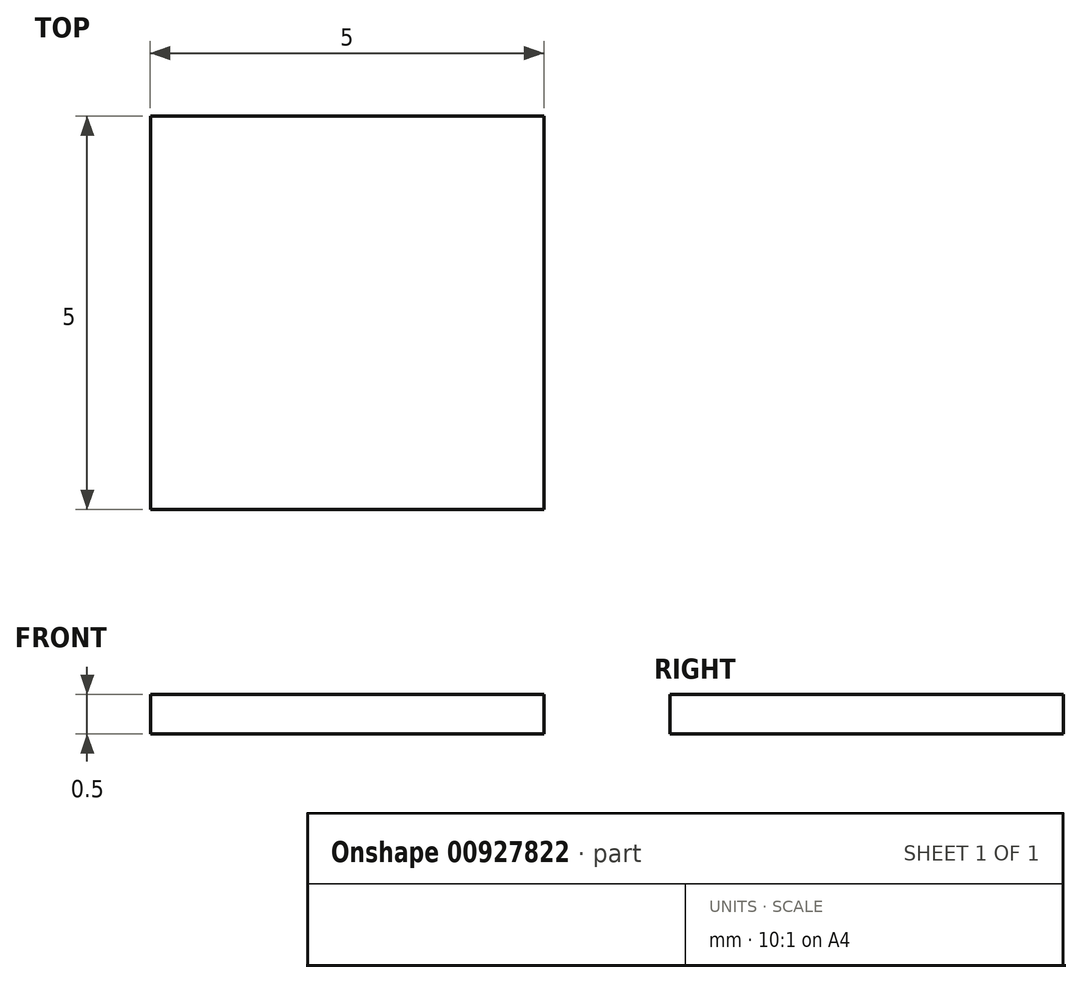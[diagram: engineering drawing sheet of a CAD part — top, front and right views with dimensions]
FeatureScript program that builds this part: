
annotation { "Feature Type Name" : "Feature", "Feature Type Description" : "" }
export const myFeature = defineFeature(function(context is Context, id is Id, definition is map)
    precondition{}
    {
        {
            var Q0;
            Q0=qCreatedBy(makeId("Top.planeOp"),FACE);
            var sketch = newSketch(context, id + "F0", { "sketchPlane" : qUnion([Q0])});
            skLineSegment(sketch, "E0.bottom", {"start": v(51.03, 42.4) * mm, "end": v(56.03, 42.4) * mm});
            skLineSegment(sketch, "E0.top", {"start": v(51.03, 37.4) * mm, "end": v(56.03, 37.4) * mm});
            skLineSegment(sketch, "E0.left", {"start": v(51.03, 42.4) * mm, "end": v(51.03, 37.4) * mm});
            skLineSegment(sketch, "E0.right", {"start": v(56.03, 42.4) * mm, "end": v(56.03, 37.4) * mm});
            skSolve(sketch);
        }
        {
            var Q0;
            Q0=makeQuery(id+"F0.imprint","IMPRINT",FACE,{"disambiguationData":[TD([[makeQuery(id+"F0.imprint","IMPRINT",EDGE,{"derivedFrom":sQuery(id+"F0.wireOp",EDGE,"E0.bottom")}),-1.0]])]});
            extrude(context, id + "F1", {"entities" : qUnion([Q0]), "depth" : .5 * mm, "offsetDistance" : 25 * mm});
        }
    });
